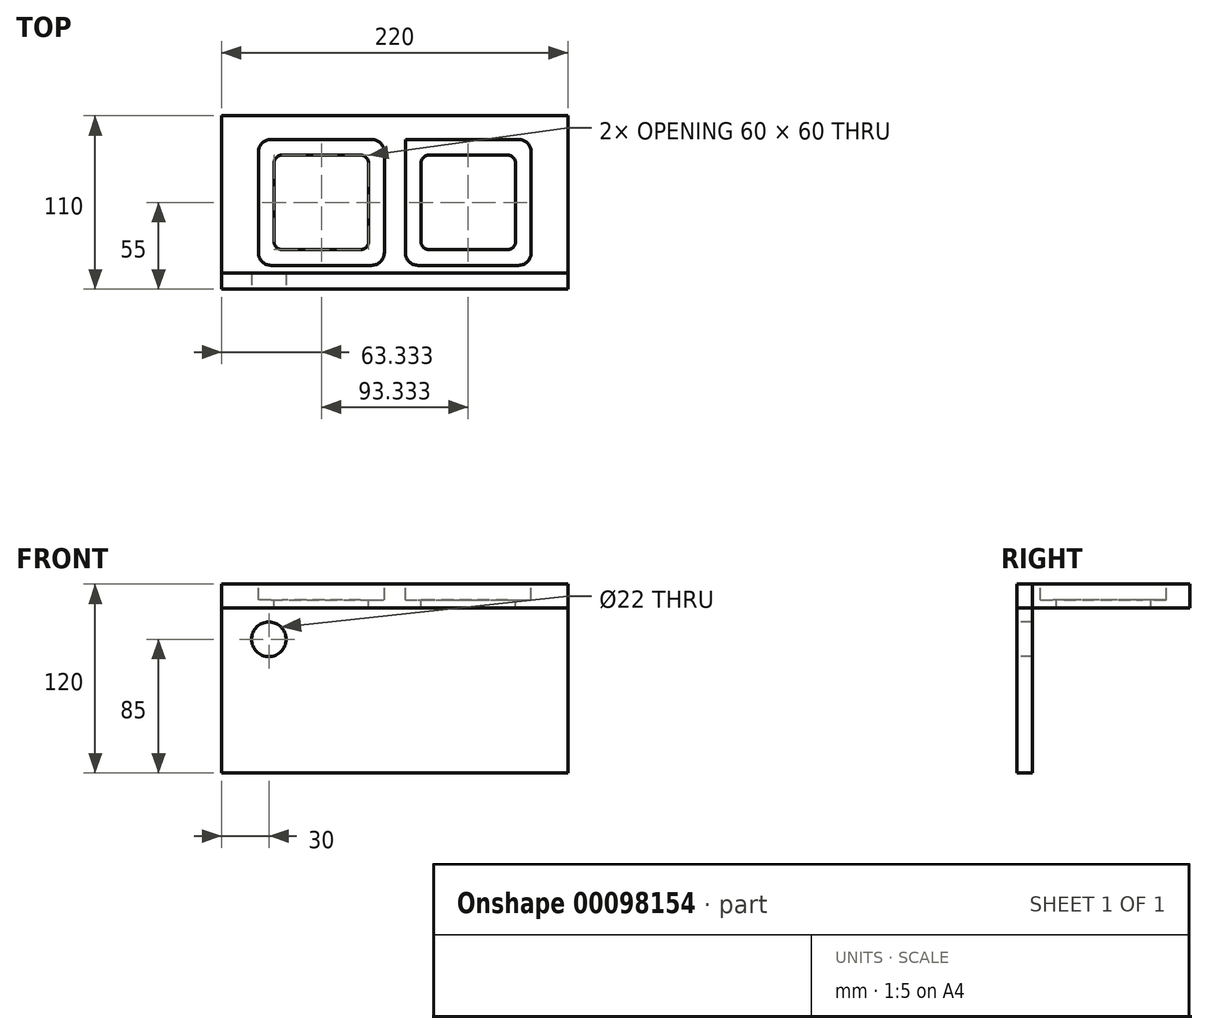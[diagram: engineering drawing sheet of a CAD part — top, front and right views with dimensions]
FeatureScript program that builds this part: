
annotation { "Feature Type Name" : "Feature", "Feature Type Description" : "" }
export const myFeature = defineFeature(function(context is Context, id is Id, definition is map)
    precondition{}
    {
        {
            var Q0;
            Q0=qCreatedBy(makeId("Right.planeOp"),FACE);
            cPlane(context, id + "F0", {"entities" : qUnion([Q0]), "cplaneType" : CPlaneType.OFFSET, "offset" : 220 * mm, "width" : 150 * mm, "height" : 150 * mm});
        }
        {
            var Q0;
            Q0=qCreatedBy(makeId("Top.planeOp"),FACE);
            cPlane(context, id + "F1", {"entities" : qUnion([Q0]), "cplaneType" : CPlaneType.OFFSET, "offset" : 120 * mm, "width" : 150 * mm, "height" : 150 * mm});
        }
        {
            var Q0;
            Q0=qCreatedBy(id+"F0.planeOp",FACE);
            var sketch = newSketch(context, id + "F2", { "sketchPlane" : qUnion([Q0])});
            skLineSegment(sketch, "E0", {"start": v(0, 0) * mm, "end": v(110, 0) * mm});
            skLineSegment(sketch, "E1", {"start": v(110, 0) * mm, "end": v(110, 120) * mm});
            skLineSegment(sketch, "E2", {"start": v(110, 120) * mm, "end": v(0, 120) * mm});
            skLineSegment(sketch, "E3", {"start": v(0, 120) * mm, "end": v(0, 0) * mm});
            skLineSegment(sketch, "E4", {"start": v(55, 120) * mm, "end": v(55, 0) * mm, "construction": true});
            skLineSegment(sketch, "E5", {"start": v(0, 60) * mm, "end": v(110, 60) * mm, "construction": true});
            skPoint(sketch, "E6", {"position": v(55, 60) * mm});
            skLineSegment(sketch, "E7.bottom", {"start": v(10, 110) * mm, "end": v(100, 110) * mm});
            skLineSegment(sketch, "E7.top", {"start": v(10, 10) * mm, "end": v(100, 10) * mm});
            skLineSegment(sketch, "E7.left", {"start": v(10, 110) * mm, "end": v(10, 10) * mm});
            skLineSegment(sketch, "E7.right", {"start": v(100, 110) * mm, "end": v(100, 10) * mm});
            skLineSegment(sketch, "E8", {"start": v(10, 65) * mm, "end": v(100, 65) * mm});
            skLineSegment(sketch, "E9", {"start": v(10, 55) * mm, "end": v(100, 55) * mm});
            skSolve(sketch);
        }
        {
            var Q0;
            Q0=qCreatedBy(makeId("Front.planeOp"),FACE);
            var sketch = newSketch(context, id + "F3", { "sketchPlane" : qUnion([Q0])});
            skLineSegment(sketch, "E10", {"start": v(0, 120) * mm, "end": v(0, 0) * mm});
            skLineSegment(sketch, "E11", {"start": v(0, 0) * mm, "end": v(220, 0) * mm});
            skLineSegment(sketch, "E12", {"start": v(220, 0) * mm, "end": v(220, 120) * mm});
            skLineSegment(sketch, "E13", {"start": v(220, 120) * mm, "end": v(0, 120) * mm});
            skLineSegment(sketch, "E14.bottom", {"start": v(30, 85) * mm, "end": v(95, 85) * mm, "construction": true});
            skLineSegment(sketch, "E14.top", {"start": v(30, 35) * mm, "end": v(95, 35) * mm, "construction": true});
            skLineSegment(sketch, "E14.left", {"start": v(30, 85) * mm, "end": v(30, 35) * mm, "construction": true});
            skLineSegment(sketch, "E14.right", {"start": v(95, 85) * mm, "end": v(95, 35) * mm, "construction": true});
            skLineSegment(sketch, "E15", {"start": v(95, 85) * mm, "end": v(160, 85) * mm, "construction": true});
            skLineSegment(sketch, "E16", {"start": v(160, 85) * mm, "end": v(160, 35) * mm, "construction": true});
            skLineSegment(sketch, "E17", {"start": v(160, 35) * mm, "end": v(95, 35) * mm, "construction": true});
            skLineSegment(sketch, "E18", {"start": v(30, 85) * mm, "end": v(30, 120) * mm, "construction": true});
            skLineSegment(sketch, "E19", {"start": v(30, 35) * mm, "end": v(30, 0) * mm, "construction": true});
            skSolve(sketch);
        }
        {
            var Q0;
            Q0=qCreatedBy(makeId("Front.planeOp"),FACE);
            var sketch = newSketch(context, id + "F4", { "sketchPlane" : qUnion([Q0])});
            skCircle(sketch, "E20", {"center": v(30, 85) * mm, "radius": 11 * mm});
            skSolve(sketch);
        }
        {
            var Q0;
            Q0=qCreatedBy(id+"F1.planeOp",FACE);
            var sketch = newSketch(context, id + "F5", { "sketchPlane" : qUnion([Q0])});
            skLineSegment(sketch, "E21", {"start": v(0, 0) * mm, "end": v(0, 110) * mm});
            skLineSegment(sketch, "E22", {"start": v(0, 110) * mm, "end": v(220, 110) * mm});
            skLineSegment(sketch, "E23", {"start": v(220, 110) * mm, "end": v(220, 0) * mm});
            skLineSegment(sketch, "E24", {"start": v(220, 0) * mm, "end": v(0, 0) * mm});
            skLineSegment(sketch, "E25.bottom", {"start": v(33.33, 85) * mm, "end": v(93.33, 85) * mm});
            skLineSegment(sketch, "E25.top", {"start": v(33.33, 25) * mm, "end": v(93.33, 25) * mm});
            skLineSegment(sketch, "E25.left", {"start": v(33.33, 85) * mm, "end": v(33.33, 25) * mm});
            skLineSegment(sketch, "E25.right", {"start": v(93.33, 85) * mm, "end": v(93.33, 25) * mm});
            skLineSegment(sketch, "E26.bottom", {"start": v(126.67, 85) * mm, "end": v(186.67, 85) * mm});
            skLineSegment(sketch, "E26.top", {"start": v(126.67, 25) * mm, "end": v(186.67, 25) * mm});
            skLineSegment(sketch, "E26.left", {"start": v(126.67, 85) * mm, "end": v(126.67, 25) * mm});
            skLineSegment(sketch, "E26.right", {"start": v(186.67, 85) * mm, "end": v(186.67, 25) * mm});
            skLineSegment(sketch, "E27", {"start": v(33.33, 85) * mm, "end": v(0, 85) * mm, "construction": true});
            skLineSegment(sketch, "E28", {"start": v(186.67, 85) * mm, "end": v(220, 85) * mm, "construction": true});
            skLineSegment(sketch, "E29", {"start": v(33.33, 85) * mm, "end": v(33.33, 110) * mm, "construction": true});
            skLineSegment(sketch, "E30", {"start": v(186.67, 25) * mm, "end": v(186.67, 0) * mm, "construction": true});
            skLineSegment(sketch, "E31", {"start": v(93.33, 85) * mm, "end": v(126.67, 85) * mm, "construction": true});
            skSolve(sketch);
        }
        {
            var Q0;
            Q0=makeQuery(id+"F5.imprint","IMPRINT",FACE,{"disambiguationData":[TD([[makeQuery(id+"F5.imprint","IMPRINT",EDGE,{"derivedFrom":sQuery(id+"F5.wireOp",EDGE,"E21")}),-1.0]])]});
            extrude(context, id + "F6", {"entities" : qUnion([Q0]), "oppositeDirection" : true, "depth" : 15 * mm});
        }
        {
            var Q0;
            Q0=makeQuery(id+"F6.opExtrude","SWEPT_EDGE",EDGE,{"disambiguationData":[OSD([sQuery(id+"F5.wireOp",EDGE,"E25.bottom"),sQuery(id+"F5.wireOp",EDGE,"E25.right")])]});
            var Q1;
            Q1=makeQuery(id+"F6.opExtrude","SWEPT_EDGE",EDGE,{"disambiguationData":[OSD([sQuery(id+"F5.wireOp",EDGE,"E26.bottom"),sQuery(id+"F5.wireOp",EDGE,"E26.right")])]});
            var Q2;
            Q2=makeQuery(id+"F6.opExtrude","SWEPT_EDGE",EDGE,{"disambiguationData":[OSD([sQuery(id+"F5.wireOp",EDGE,"E25.bottom"),sQuery(id+"F5.wireOp",EDGE,"E25.left")])]});
            var Q3;
            Q3=makeQuery(id+"F6.opExtrude","SWEPT_EDGE",EDGE,{"disambiguationData":[OSD([sQuery(id+"F5.wireOp",EDGE,"E25.top"),sQuery(id+"F5.wireOp",EDGE,"E25.left")])]});
            var Q4;
            Q4=makeQuery(id+"F6.opExtrude","SWEPT_EDGE",EDGE,{"disambiguationData":[OSD([sQuery(id+"F5.wireOp",EDGE,"E25.top"),sQuery(id+"F5.wireOp",EDGE,"E25.right")])]});
            var Q5;
            Q5=makeQuery(id+"F6.opExtrude","SWEPT_EDGE",EDGE,{"disambiguationData":[OSD([sQuery(id+"F5.wireOp",EDGE,"E26.top"),sQuery(id+"F5.wireOp",EDGE,"E26.right")])]});
            var Q6;
            Q6=makeQuery(id+"F6.opExtrude","SWEPT_EDGE",EDGE,{"disambiguationData":[OSD([sQuery(id+"F5.wireOp",EDGE,"E26.top"),sQuery(id+"F5.wireOp",EDGE,"E26.left")])]});
            var Q7;
            Q7=makeQuery(id+"F6.opExtrude","SWEPT_EDGE",EDGE,{"disambiguationData":[OSD([sQuery(id+"F5.wireOp",EDGE,"E26.bottom"),sQuery(id+"F5.wireOp",EDGE,"E26.left")])]});
            fillet(context, id + "F7", {"entities" : qUnion([Q0, Q1, Q2, Q3, Q4, Q5, Q6, Q7]), "radius" : 5 * mm, "tangentPropagation" : true, "allowEdgeOverflow" : false});
        }
        {
            var Q0;
            Q0=qCreatedBy(id+"F1.planeOp",FACE);
            var sketch = newSketch(context, id + "F8", { "sketchPlane" : qUnion([Q0])});
            skLineSegment(sketch, "E32.0", {"start": v(23.33, 95) * mm, "end": v(103.33, 95) * mm});
            skLineSegment(sketch, "E32.1", {"start": v(23.33, 95) * mm, "end": v(23.33, 15) * mm});
            skLineSegment(sketch, "E32.2", {"start": v(23.33, 15) * mm, "end": v(103.33, 15) * mm});
            skLineSegment(sketch, "E32.3", {"start": v(103.33, 95) * mm, "end": v(103.33, 15) * mm});
            skLineSegment(sketch, "E33.0", {"start": v(116.67, 95) * mm, "end": v(196.67, 95) * mm});
            skLineSegment(sketch, "E33.1", {"start": v(116.67, 95) * mm, "end": v(116.67, 15) * mm});
            skLineSegment(sketch, "E33.2", {"start": v(116.67, 15) * mm, "end": v(196.67, 15) * mm});
            skLineSegment(sketch, "E33.3", {"start": v(196.67, 95) * mm, "end": v(196.67, 15) * mm});
            skSolve(sketch);
        }
        {
            var Q0;
            Q0 = qSketchRegion(id + "F8", true);
            extrude(context, id + "F9", {"entities" : qUnion([Q0]), "operationType" : NewBodyOperationType.REMOVE, "oppositeDirection" : true, "depth" : 10 * mm});
        }
        {
            var Q0;
            Q0=makeQuery(id+"F9.boolean.opBoolean","COPY",EDGE,{"derivedFrom":makeQuery(id+"F9.opExtrude","SWEPT_EDGE",EDGE,{"disambiguationData":[OSD([sQuery(id+"F8.wireOp",EDGE,"E32.0"),sQuery(id+"F8.wireOp",EDGE,"E32.3")])]})});
            var Q1;
            Q1=makeQuery(id+"F9.boolean.opBoolean","COPY",EDGE,{"derivedFrom":makeQuery(id+"F9.opExtrude","SWEPT_EDGE",EDGE,{"disambiguationData":[OSD([sQuery(id+"F8.wireOp",EDGE,"E33.0"),sQuery(id+"F8.wireOp",EDGE,"E33.3")])]})});
            var Q2;
            Q2=makeQuery(id+"F9.boolean.opBoolean","COPY",EDGE,{"derivedFrom":makeQuery(id+"F9.opExtrude","SWEPT_EDGE",EDGE,{"disambiguationData":[OSD([sQuery(id+"F8.wireOp",EDGE,"E32.0"),sQuery(id+"F8.wireOp",EDGE,"E32.1")])]})});
            var Q3;
            Q3=makeQuery(id+"F9.boolean.opBoolean","COPY",EDGE,{"derivedFrom":makeQuery(id+"F9.opExtrude","SWEPT_EDGE",EDGE,{"disambiguationData":[OSD([sQuery(id+"F8.wireOp",EDGE,"E32.1"),sQuery(id+"F8.wireOp",EDGE,"E32.2")])]})});
            var Q4;
            Q4=makeQuery(id+"F9.boolean.opBoolean","COPY",EDGE,{"derivedFrom":makeQuery(id+"F9.opExtrude","SWEPT_EDGE",EDGE,{"disambiguationData":[OSD([sQuery(id+"F8.wireOp",EDGE,"E32.2"),sQuery(id+"F8.wireOp",EDGE,"E32.3")])]})});
            var Q5;
            Q5=makeQuery(id+"F9.boolean.opBoolean","COPY",EDGE,{"derivedFrom":makeQuery(id+"F9.opExtrude","SWEPT_EDGE",EDGE,{"disambiguationData":[OSD([sQuery(id+"F8.wireOp",EDGE,"E33.2"),sQuery(id+"F8.wireOp",EDGE,"E33.3")])]})});
            var Q6;
            Q6=makeQuery(id+"F9.boolean.opBoolean","COPY",EDGE,{"derivedFrom":makeQuery(id+"F9.opExtrude","SWEPT_EDGE",EDGE,{"disambiguationData":[OSD([sQuery(id+"F8.wireOp",EDGE,"E33.1"),sQuery(id+"F8.wireOp",EDGE,"E33.2")])]})});
            fillet(context, id + "F10", {"entities" : qUnion([Q0, Q1, Q2, Q3, Q4, Q5, Q6]), "radius" : 8 * mm, "tangentPropagation" : true, "allowEdgeOverflow" : false});
        }
        {
            var Q0;
            Q0 = qSketchRegion(id + "F3", true);
            extrude(context, id + "F11", {"entities" : qUnion([Q0]), "oppositeDirection" : true, "depth" : 10 * mm});
        }
        {
            var Q0;
            Q0=makeQuery(id+"F4.imprint","IMPRINT",FACE,{"disambiguationData":[TD([[makeQuery(id+"F4.imprint","IMPRINT",EDGE,{"derivedFrom":sQuery(id+"F4.wireOp",EDGE,"E20")}),1.0]])]});
            extrude(context, id + "F12", {"entities" : qUnion([Q0]), "operationType" : NewBodyOperationType.REMOVE, "oppositeDirection" : true, "depth" : 25 * mm});
        }
    });
